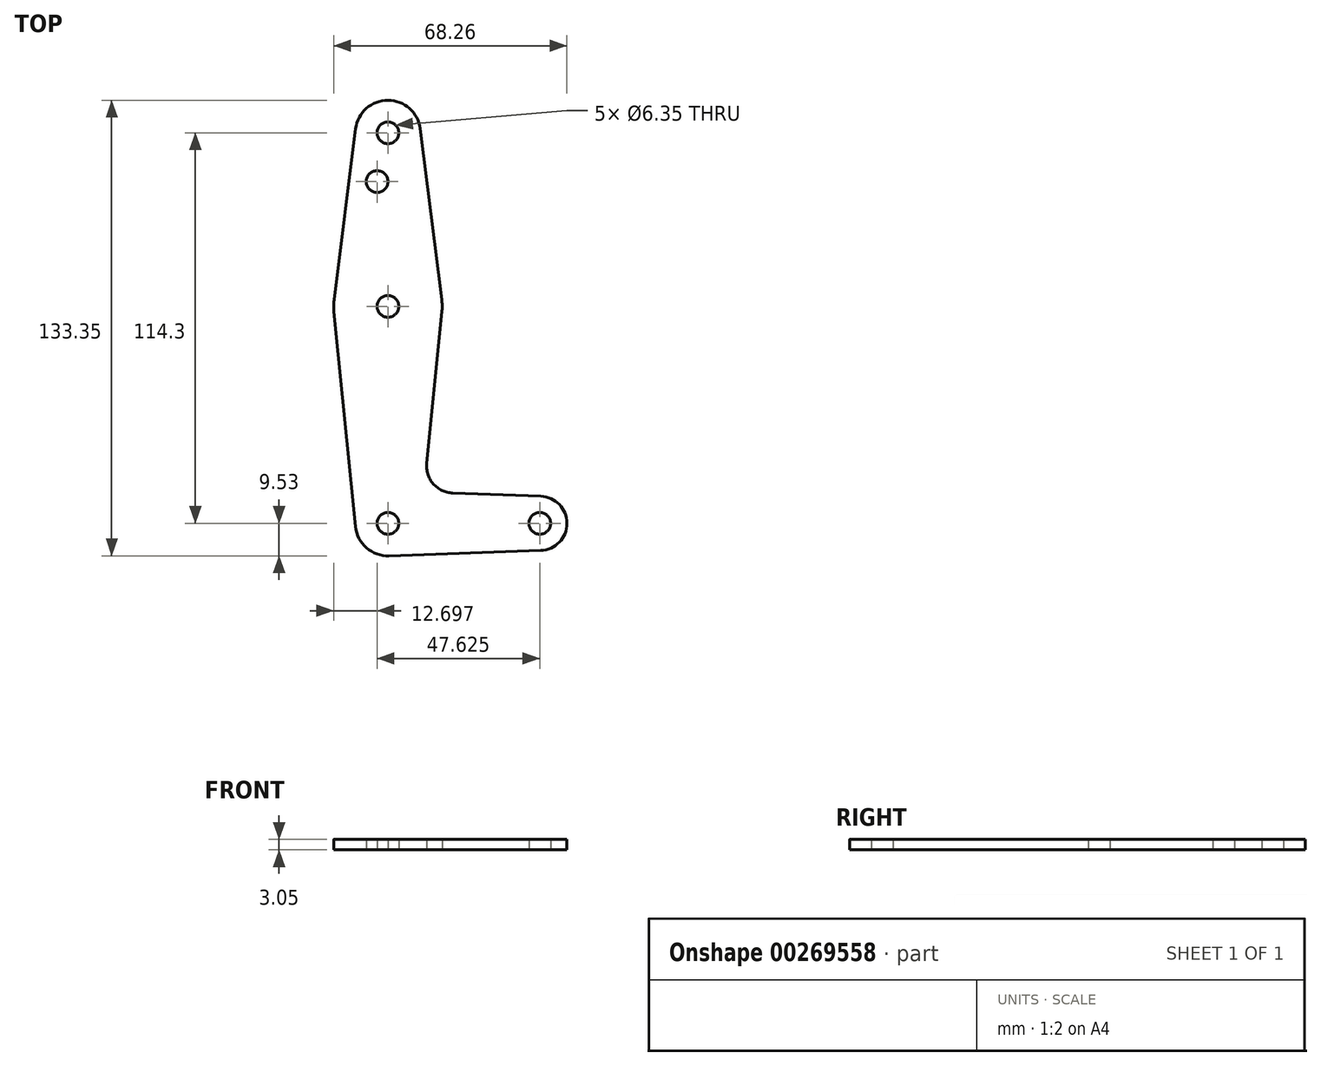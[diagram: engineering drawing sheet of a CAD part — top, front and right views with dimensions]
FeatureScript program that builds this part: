
annotation { "Feature Type Name" : "Feature", "Feature Type Description" : "" }
export const myFeature = defineFeature(function(context is Context, id is Id, definition is map)
    precondition{}
    {
        {
            var Q0;
            Q0=qCreatedBy(makeId("Top.planeOp"),FACE);
            var sketch = newSketch(context, id + "F0", { "sketchPlane" : qUnion([Q0])});
            skLineSegment(sketch, "E0", {"start": v(-11.47, 50.8) * mm, "end": v(-11.47, -63.5) * mm, "construction": true});
            skLineSegment(sketch, "E1", {"start": v(-11.47, -63.5) * mm, "end": v(32.98, -63.5) * mm, "construction": true});
            skCircle(sketch, "E2", {"center": v(-11.47, 0) * mm, "radius": 15.88 * mm});
            skCircle(sketch, "E3", {"center": v(-11.47, 50.8) * mm, "radius": 9.53 * mm});
            skCircle(sketch, "E4", {"center": v(-11.47, -63.5) * mm, "radius": 9.53 * mm});
            skCircle(sketch, "E5", {"center": v(32.98, -63.5) * mm, "radius": 7.94 * mm});
            skLineSegment(sketch, "E6", {"start": v(-20.92, 52) * mm, "end": v(-27.22, 1.98) * mm});
            skLineSegment(sketch, "E7", {"start": v(-2.02, 52) * mm, "end": v(4.28, 1.98) * mm});
            skLineSegment(sketch, "E8", {"start": v(-27.26, -1.59) * mm, "end": v(-20.95, -64.45) * mm});
            skLineSegment(sketch, "E9", {"start": v(-0.13, -45.9) * mm, "end": v(4.33, -1.59) * mm});
            skLineSegment(sketch, "E10", {"start": v(-11.13, -73.02) * mm, "end": v(33.27, -71.43) * mm});
            skLineSegment(sketch, "E11", {"start": v(7.5, -54.65) * mm, "end": v(33.27, -55.57) * mm});
            skArc(sketch, "E12.filletArc", {"start": v(-0.13, -45.9) * mm, "mid": v(1.8, -51.93) * mm, "end": v(7.5, -54.65) * mm});
            skCircle(sketch, "E13", {"center": v(-11.47, 50.8) * mm, "radius": 3.18 * mm});
            skCircle(sketch, "E14", {"center": v(-11.47, 0) * mm, "radius": 3.17 * mm});
            skCircle(sketch, "E15", {"center": v(-11.47, -63.5) * mm, "radius": 3.18 * mm});
            skCircle(sketch, "E16", {"center": v(32.98, -63.5) * mm, "radius": 3.18 * mm});
            skCircle(sketch, "E17", {"center": v(-14.64, 36.53) * mm, "radius": 3.18 * mm});
            skSolve(sketch);
        }
        {
            var Q0;
            Q0 = qSketchRegion(id + "F0", true);
            extrude(context, id + "F1", {"entities" : qUnion([Q0]), "depth" : 3.05 * mm});
        }
    });
